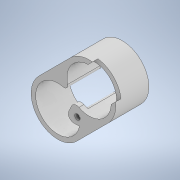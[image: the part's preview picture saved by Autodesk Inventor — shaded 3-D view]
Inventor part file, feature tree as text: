
AUTODESK INVENTOR PART (.ipt)
format: ipt  version: 2020 (Build 240168000, 168)  size: 281,088 bytes
history: native  units: in
note: dims shown in document units (in); Inventor stores cm internally (conversion verified against a paired STEP export)
features: extrude x6, sketch x6, fillet x5, mirror x2
ambient origin geometry x8: Origin, YZ Plane, XZ Plane, XY Plane, X Axis, Y Axis, Z Axis, Center Point
bodies: Solid1 (feature_tree)
feature tree (19):
  extrude  "Extrusion1"  Depth=0.9606in
  extrude  "Extrusion3"  TaperAngle=45.0deg  [1 undecoded]
  extrude  "Extrusion4"  Depth=0.4134in
  extrude  "Extrusion5"  Depth=0.1181in
  fillet  "Fillet1"  Radius=0.1181in
  fillet  "Fillet2"  Radius=0.1181in
  mirror  "Mirror1"
  extrude  "Extrusion6"  Depth=0.1083in
  mirror  "Mirror2"
  fillet  "Fillet3"  Radius=0.1772in
  fillet  "Fillet4"  Radius=0.1083in
  fillet  "Fillet5"  Radius=0.6102in
  extrude  "Extrusion7"  Depth=0.2165in
  sketch  "Sketch1"  dims[d0=0.9724in d1=0.9606in]
  sketch  "Sketch6"  dims[d24=0.9606in d25=0.9606in d26=0.1772in d27=0.1083in d28=0.0in]
  sketch  "Sketch7"  dims[d32=0.9724in d33=0.9606in d34=0.0in d35=45.0deg d36=0.0in d37=0.4134in d38=0.3346in d39=0.1181in d40=0.1181in d41=0.1181in d42=0.9606in d43=0.9606in d44=0.1772in d45=0.6102in d46=0.0in d49=0.2165in d50=0.0787in d51=0.0394in d52=0.0in d53=0.0in d54=0.9724in d55=0.9606in d56=0.0in d57=45.0deg d58=0.0in d59=0.4134in d60=0.3346in d61=0.1181in d62=0.1181in d63=0.1181in d64=0.9606in d65=0.9606in d66=0.1772in d67=0.5787in d68=0.5787in d69=1.1575in d70=0.5787in d71=0.7185in d72=0.0in d73=0.1181in d74=0.1181in d75=0.7185in d76=0.0in d77=0.0787in d78=0.0787in d79=0.0787in d80=0.3543in d81=0.3543in d82=1.1811in d83=0.7087in d84=0.1181in d85=0.0in]
  sketch  "Sketch3"  dims[d2=0.0in d3=45.0deg]
  sketch  "Sketch4"  dims[d4=0.0in d5=0.4134in]
  sketch  "Sketch5"  dims[d20=0.3346in d21=0.1181in d22=0.1181in d23=0.1181in]
note: 1 required parameter value undecoded (feature->parameter linkage not recoverable at this tier; creation-order binding heuristic only, values carry confidence <= 0.55)
